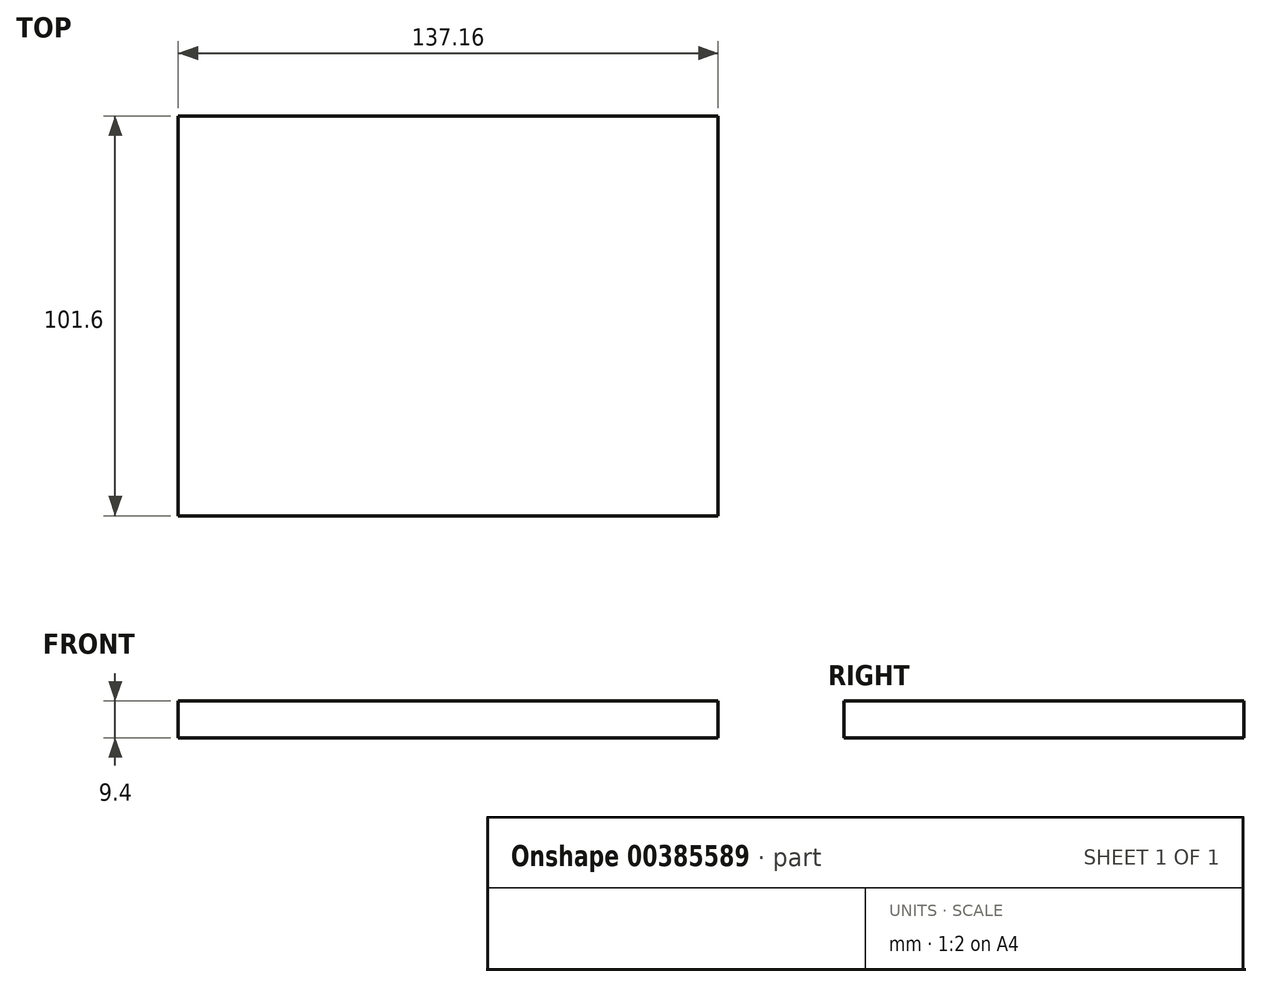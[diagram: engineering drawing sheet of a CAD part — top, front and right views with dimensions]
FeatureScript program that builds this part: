
annotation { "Feature Type Name" : "Feature", "Feature Type Description" : "" }
export const myFeature = defineFeature(function(context is Context, id is Id, definition is map)
    precondition{}
    {
        {
            var Q0;
            Q0=qCreatedBy(makeId("Front.planeOp"),FACE);
            var sketch = newSketch(context, id + "F0", { "sketchPlane" : qUnion([Q0])});
            skLineSegment(sketch, "E0.bottom", {"start": v(0, 0) * mm, "end": v(137.16, 0) * mm});
            skLineSegment(sketch, "E0.top", {"start": v(0, 9.4) * mm, "end": v(137.16, 9.4) * mm});
            skLineSegment(sketch, "E0.left", {"start": v(0, 0) * mm, "end": v(0, 9.4) * mm});
            skLineSegment(sketch, "E0.right", {"start": v(137.16, 0) * mm, "end": v(137.16, 9.4) * mm});
            skSolve(sketch);
        }
        {
            var Q0;
            Q0 = qSketchRegion(id + "F0", true);
            extrude(context, id + "F1", {"entities" : qUnion([Q0]), "depth" : 101.6 * mm});
        }
    });
